# Revit family: PRD_AR_ShwrFttngsPckg_F5ExtensionSet_ACXT90011
name_source: partatom
category: Specialty Equipment
units: mm (PartAtom-declared; Revit-internal decimal feet)

## family parameters
Always vertical = Yes
Cut with Voids When Loaded = No
Enable Cutting in Views = No
Maintain Annotation Orientation = No
OmniClass Number = 23.45.05.14.17.11
OmniClass Title = Shower Compartments
Part Type = Normal
Room Calculation Point = No
Round Connector Dimension = Use Diameter
Shared = No
Work Plane-Based = No

## types (1)
- ACXT9001
    AssetType = Fixed
    BIMObjectName = PRD_AR_ShowerFittingsPackage_F5ExtensionSet_ACXT9001
    BodyMaterial = <By Category>
    Category = Pr_40_20_87_75, Shower fittings package
    Default Elevation = 0 mm  [stored 0 ft]
    Description = Extension set for F5S-Therm self-closing thermostatic mixer DN 15, F5E-Therm and F3E-Therm thermostatic mixer DN 15, electronic control, for wall mounting, for depth adjustment 25 mm.
    Export Type to IFC As = IfcSanitaryTerminalType
    Features = For wall mounting, for depth adjustment 25 mm.
    IfcExportAs = IfcSanitaryTerminalType
    IfcExportType = USERDEFINED
    Manufacturer = KWC Group Management AG
    ManufacturerName = KWC Group Management AG
    ManufacturerURL = www.kwc-professional.com
    Model = ACXT9001
    ModelNumber = 2030067889
    ModelReference = ACXT9001
    NBSDescription = Shower fittings package
    NBSReference = 45-35-70/330
    Name = F5 Extension set ACXT9001
    NominalDepth = 25 mm  [stored 0.082021 ft]
    NominalHeight = 61 mm  [stored 0.200131 ft]
    NominalLength = 61 mm  [stored 0.200131 ft]
    NominalWidth = 65 mm  [stored 0.213255 ft]
    ProductInformation = http://pim.kwc.com
    Quantity = 1
    QuantityUom = piece
    Shape = cuboid
    Size = 15
    Status = New
    Type IFC Predefined Type = USERDEFINED
    URL = www.kwc-professional.com
    Uniclass2015Code = Pr_40_20_87_75
    Uniclass2015Title = Shower fittings package
    Uniclass2015Version = Products v1.36
    Version = 1

note: [stored X ft] marks values corroborated as IEEE doubles in the binary element streams (Revit-internal decimal feet)

## geometry (parser evidence)
native form markers: Sweep x5
no freeform markers — native parametric forms only
